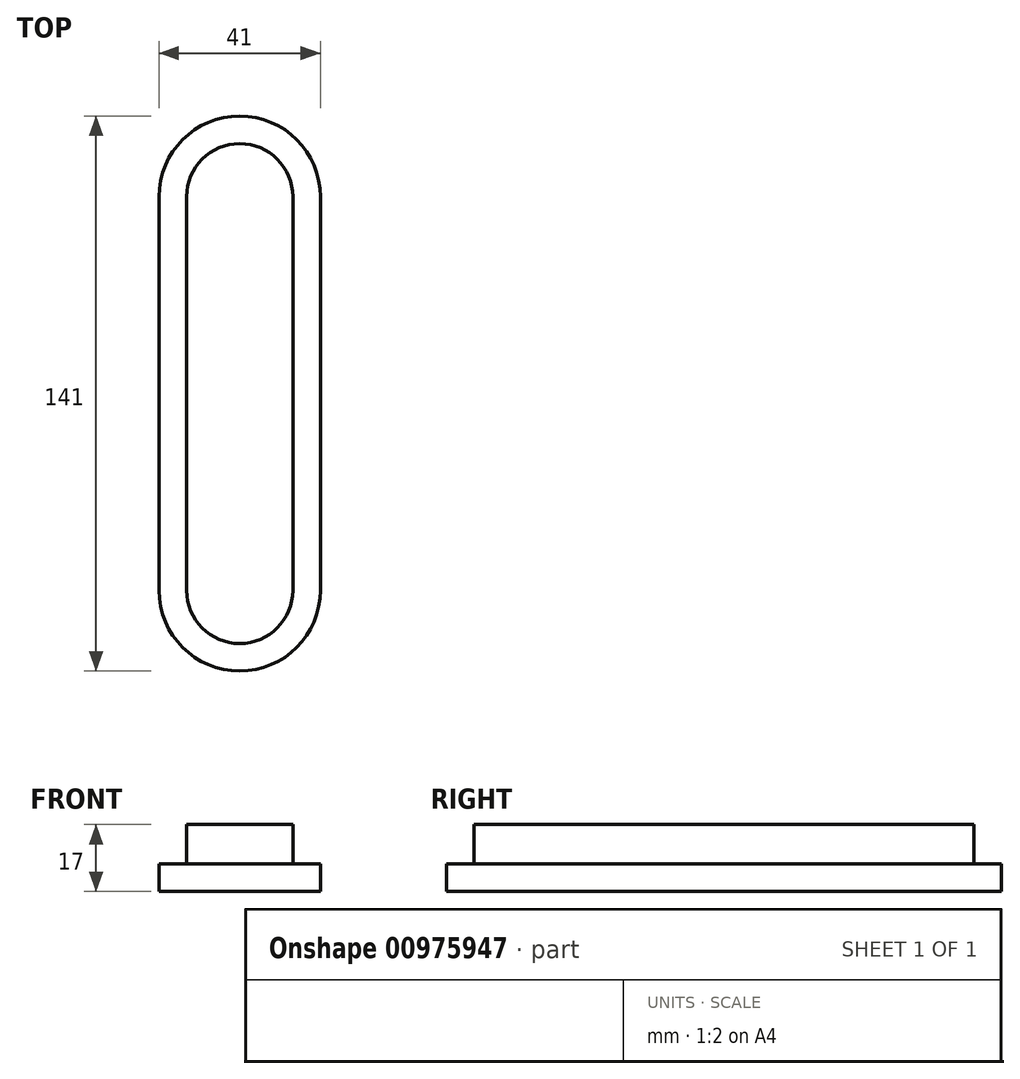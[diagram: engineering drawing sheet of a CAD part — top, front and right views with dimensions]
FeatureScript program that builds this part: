
annotation { "Feature Type Name" : "Feature", "Feature Type Description" : "" }
export const myFeature = defineFeature(function(context is Context, id is Id, definition is map)
    precondition{}
    {
        {
            var Q0;
            Q0=qCreatedBy(makeId("Top.planeOp"),FACE);
            var sketch = newSketch(context, id + "F0", { "sketchPlane" : qUnion([Q0])});
            skLineSegment(sketch, "E0", {"start": v(0, 63.5) * mm, "end": v(0, -63.5) * mm, "construction": true});
            skLineSegment(sketch, "E1", {"start": v(-13.5, 0) * mm, "end": v(13.5, 0) * mm, "construction": true});
            skArc(sketch, "E2", {"start": v(-13.5, -50) * mm, "mid": v(0, -63.5) * mm, "end": v(13.5, -50) * mm});
            skArc(sketch, "E3.MirrorCS", {"start": v(-13.5, 50) * mm, "mid": v(0, 63.5) * mm, "end": v(13.5, 50) * mm});
            skLineSegment(sketch, "E4", {"start": v(-13.5, 50) * mm, "end": v(-13.5, -50) * mm});
            skLineSegment(sketch, "E5", {"start": v(13.5, 50) * mm, "end": v(13.5, -50) * mm});
            skSolve(sketch);
        }
        {
            var Q0;
            Q0 = qSketchRegion(id + "F0", true);
            extrude(context, id + "F1", {"entities" : qUnion([Q0]), "depth" : 10 * mm, "offsetDistance" : 25 * mm});
        }
        {
            var Q0;
            Q0=makeQuery(id+"F1.opExtrude","CAP_FACE",FACE,{"disambiguationData":[OSD([sQuery(id+"F0.wireOp",EDGE,"E2"),sQuery(id+"F0.wireOp",EDGE,"E3.MirrorCS"),sQuery(id+"F0.wireOp",EDGE,"E4"),sQuery(id+"F0.wireOp",EDGE,"E5")])],"isStart":true});
            var sketch = newSketch(context, id + "F2", { "sketchPlane" : qUnion([Q0])});
            skArc(sketch, "E6.0", {"start": v(-20.5, 50) * mm, "mid": v(0, 70.5) * mm, "end": v(20.5, 50) * mm});
            skLineSegment(sketch, "E6.1", {"start": v(-20.5, -50) * mm, "end": v(-20.5, 50) * mm});
            skArc(sketch, "E6.2", {"start": v(-20.5, -50) * mm, "mid": v(0, -70.5) * mm, "end": v(20.5, -50) * mm});
            skLineSegment(sketch, "E6.3", {"start": v(20.5, -50) * mm, "end": v(20.5, 50) * mm});
            skSolve(sketch);
        }
        {
            var Q0;
            Q0 = qSketchRegion(id + "F2", true);
            extrude(context, id + "F3", {"entities" : qUnion([Q0]), "operationType" : NewBodyOperationType.ADD, "depth" : 7 * mm, "offsetDistance" : 25 * mm});
        }
    });
